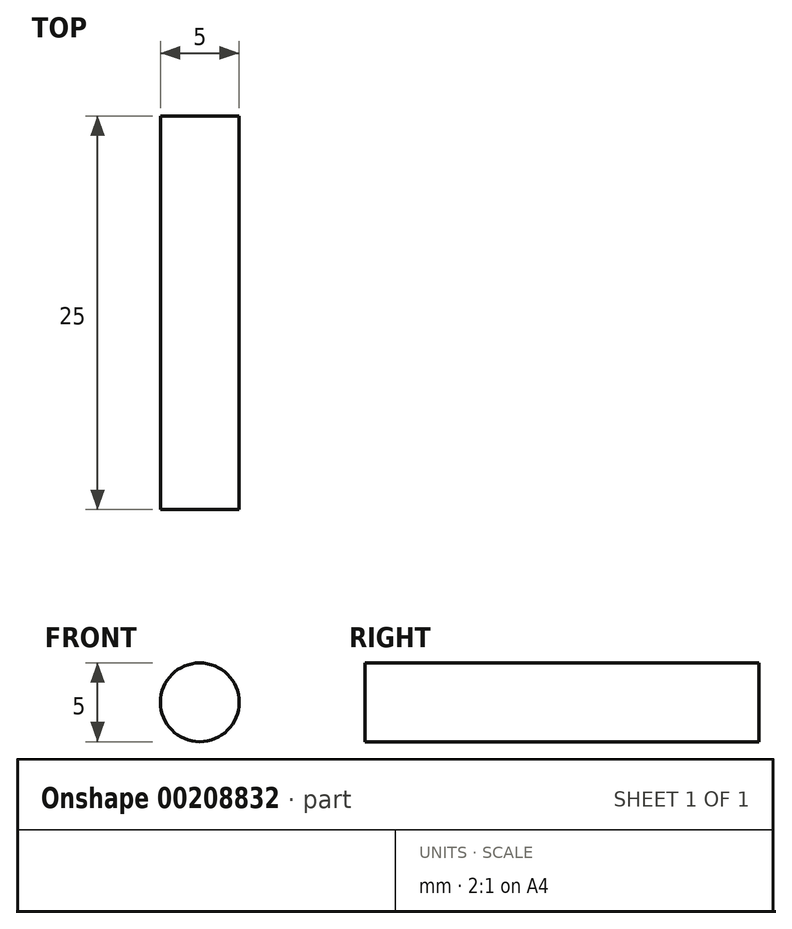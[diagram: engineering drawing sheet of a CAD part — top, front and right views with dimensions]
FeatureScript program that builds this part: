
annotation { "Feature Type Name" : "Feature", "Feature Type Description" : "" }
export const myFeature = defineFeature(function(context is Context, id is Id, definition is map)
    precondition{}
    {
        {
            var Q0;
            Q0=qCreatedBy(makeId("Front.planeOp"),FACE);
            var sketch = newSketch(context, id + "F0", { "sketchPlane" : qUnion([Q0])});
            skCircle(sketch, "E0", {"center": v(0, 0) * mm, "radius": 2.5 * mm});
            skSolve(sketch);
        }
        {
            var Q0;
            Q0=sQuery(id+"F0.wireOp",EDGE,"E0");
            extrude(context, id + "F1", {"bodyType" : ToolBodyType.SURFACE, "surfaceEntities" : qUnion([Q0]), "depth" : 25 * mm});
        }
    });
